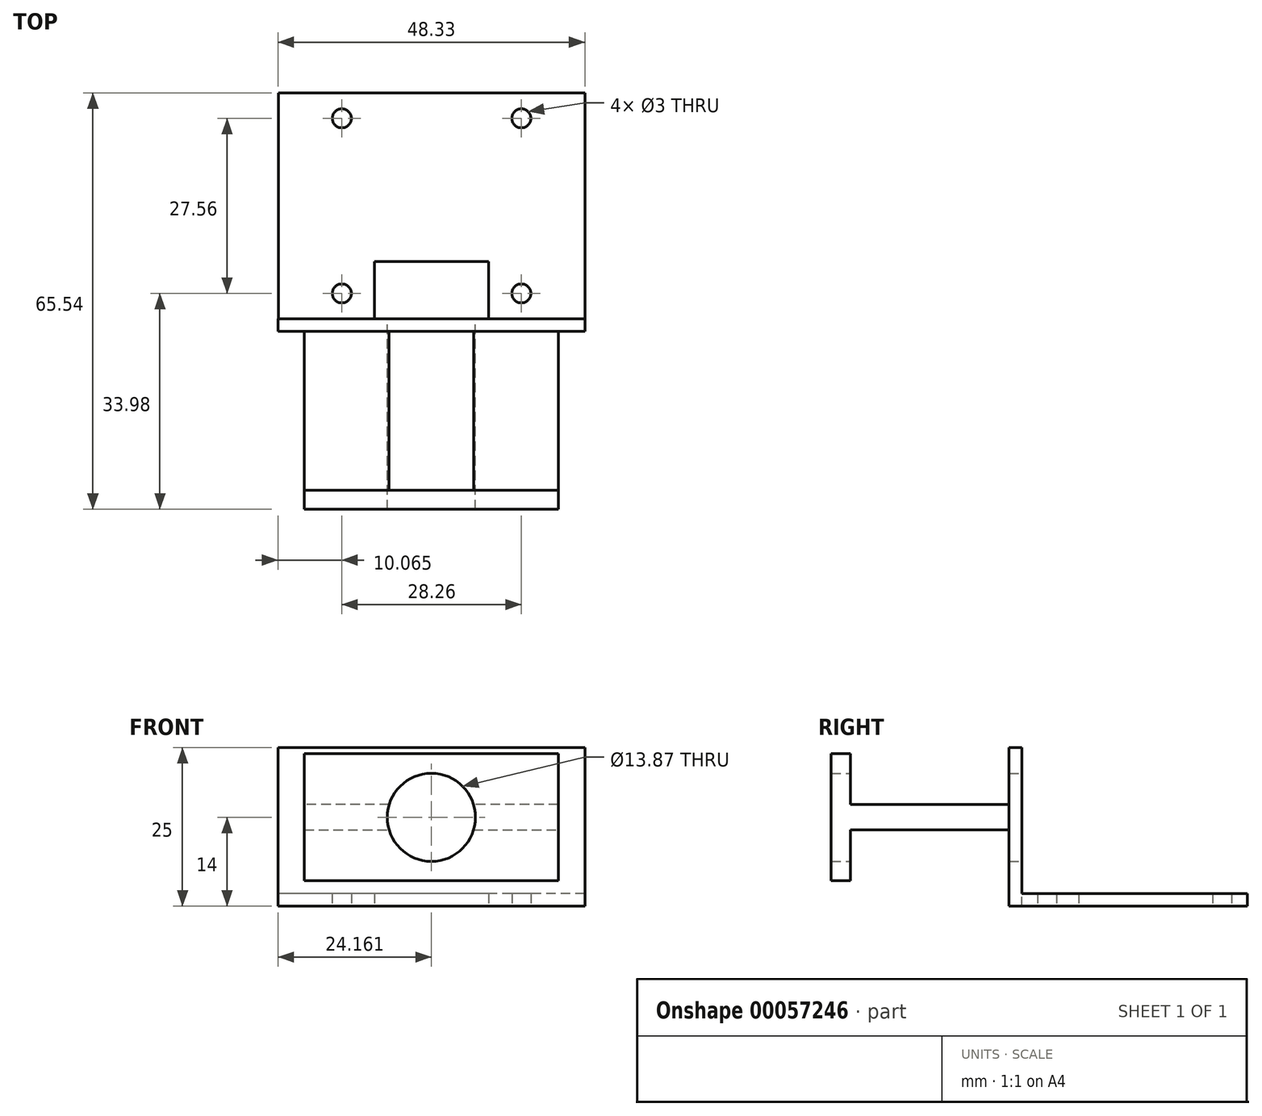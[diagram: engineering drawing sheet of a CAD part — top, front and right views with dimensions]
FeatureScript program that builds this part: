
annotation { "Feature Type Name" : "Feature", "Feature Type Description" : "" }
export const myFeature = defineFeature(function(context is Context, id is Id, definition is map)
    precondition{}
    {
        {
            var Q0;
            Q0=qCreatedBy(makeId("Top.planeOp"),FACE);
            var sketch = newSketch(context, id + "F0", { "sketchPlane" : qUnion([Q0])});
            skLineSegment(sketch, "E0.bottom", {"start": v(25, 16.6) * mm, "end": v(-23.25, 16.6) * mm});
            skLineSegment(sketch, "E0.top", {"start": v(25, -18.96) * mm, "end": v(-23.25, -18.96) * mm});
            skLineSegment(sketch, "E0.left", {"start": v(25, 16.6) * mm, "end": v(25, -18.96) * mm});
            skLineSegment(sketch, "E0.right", {"start": v(-23.25, 16.6) * mm, "end": v(-23.25, -18.96) * mm});
            skCircle(sketch, "E1", {"center": v(-13.25, 12.6) * mm, "radius": 1.5 * mm});
            skCircle(sketch, "E2", {"center": v(15, 12.6) * mm, "radius": 1.5 * mm});
            skLineSegment(sketch, "E3", {"start": v(-13.25, 16.6) * mm, "end": v(-13.25, 12.6) * mm, "construction": true});
            skLineSegment(sketch, "E4", {"start": v(-13.25, 12.6) * mm, "end": v(-23.25, 12.6) * mm, "construction": true});
            skLineSegment(sketch, "E5", {"start": v(15, 12.6) * mm, "end": v(15, 16.6) * mm, "construction": true});
            skLineSegment(sketch, "E6", {"start": v(15, 12.6) * mm, "end": v(25, 12.6) * mm, "construction": true});
            skCircle(sketch, "E7", {"center": v(-13.25, -14.96) * mm, "radius": 1.5 * mm});
            skCircle(sketch, "E8", {"center": v(15, -14.96) * mm, "radius": 1.5 * mm});
            skLineSegment(sketch, "E9", {"start": v(-13.25, -14.96) * mm, "end": v(-23.25, -14.96) * mm, "construction": true});
            skLineSegment(sketch, "E10", {"start": v(-13.25, -14.96) * mm, "end": v(-13.25, -18.96) * mm, "construction": true});
            skLineSegment(sketch, "E11", {"start": v(15, -14.96) * mm, "end": v(25, -14.96) * mm, "construction": true});
            skLineSegment(sketch, "E12", {"start": v(15, -14.96) * mm, "end": v(15, -18.96) * mm, "construction": true});
            skSolve(sketch);
        }
        {
            var Q0;
            Q0=makeQuery(id+"F0.imprint","IMPRINT",FACE,{"disambiguationData":[TD([[makeQuery(id+"F0.imprint","IMPRINT",EDGE,{"derivedFrom":sQuery(id+"F0.wireOp",EDGE,"E0.bottom")}),1.0]])]});
            extrude(context, id + "F1", {"entities" : qUnion([Q0]), "depth" : 2 * mm});
        }
        {
            var Q0;
            Q0=qCreatedBy(makeId("Top.planeOp"),FACE);
            var sketch = newSketch(context, id + "F2", { "sketchPlane" : qUnion([Q0])});
            skLineSegment(sketch, "E13.bottom", {"start": v(-23.32, -18.94) * mm, "end": v(25, -18.94) * mm});
            skLineSegment(sketch, "E13.top", {"start": v(-23.32, -20.94) * mm, "end": v(25, -20.94) * mm});
            skLineSegment(sketch, "E13.left", {"start": v(-23.32, -18.94) * mm, "end": v(-23.32, -20.94) * mm});
            skLineSegment(sketch, "E13.right", {"start": v(25, -18.94) * mm, "end": v(25, -20.94) * mm});
            skSolve(sketch);
        }
        {
            var Q0;
            Q0 = qSketchRegion(id + "F2", true);
            extrude(context, id + "F3", {"entities" : qUnion([Q0]), "operationType" : NewBodyOperationType.ADD, "depth" : 25 * mm});
        }
        {
            var Q0;
            Q0=qCreatedBy(makeId("Top.planeOp"),FACE);
            cPlane(context, id + "F4", {"entities" : qUnion([Q0]), "cplaneType" : CPlaneType.OFFSET, "offset" : 4 * mm, "oppositeDirection" : true, "width" : 150 * mm, "height" : 150 * mm});
        }
        {
            var Q0;
            Q0=makeQuery(id+"F7aZyVxxDA95Y1x_5.opBoolean","MERGE",FACE,{"derivedFrom":[makeQuery(id+"F1.opExtrude","CAP_FACE",FACE,{"disambiguationData":[OSD([sQuery(id+"F0.wireOp",EDGE,"E0.bottom"),sQuery(id+"F0.wireOp",EDGE,"E0.top"),sQuery(id+"F0.wireOp",EDGE,"E0.left"),sQuery(id+"F0.wireOp",EDGE,"E0.right"),sQuery(id+"F0.wireOp",EDGE,"E1"),sQuery(id+"F0.wireOp",EDGE,"E2"),sQuery(id+"F0.wireOp",EDGE,"E7"),sQuery(id+"F0.wireOp",EDGE,"E8")])],"isStart":true}),makeQuery(id+"F3.opExtrude","CAP_FACE",FACE,{"disambiguationData":[OSD([sQuery(id+"F2.wireOp",EDGE,"E13.bottom"),sQuery(id+"F2.wireOp",EDGE,"E13.top"),sQuery(id+"F2.wireOp",EDGE,"E13.left"),sQuery(id+"F2.wireOp",EDGE,"E13.right")])],"isStart":true})]});
            var sketch = newSketch(context, id + "F5", { "sketchPlane" : qUnion([Q0])});
            skLineSegment(sketch, "E14.bottom", {"start": v(-8.12, 9.94) * mm, "end": v(9.88, 9.94) * mm});
            skLineSegment(sketch, "E14.top", {"start": v(-8.12, 18.94) * mm, "end": v(9.88, 18.94) * mm});
            skLineSegment(sketch, "E14.left", {"start": v(-8.12, 9.94) * mm, "end": v(-8.12, 18.94) * mm});
            skLineSegment(sketch, "E14.right", {"start": v(9.88, 9.94) * mm, "end": v(9.88, 18.94) * mm});
            skLineSegment(sketch, "E15", {"start": v(-23.25, 18.94) * mm, "end": v(25, 18.94) * mm, "construction": true});
            skLineSegment(sketch, "E16", {"start": v(25, 18.94) * mm, "end": v(25.39, 18.73) * mm, "construction": true});
            skPoint(sketch, "E17", {"position": v(0.88, 18.94) * mm});
            skSolve(sketch);
        }
        {
            var Q0;
            Q0 = qSketchRegion(id + "F5", true);
            extrude(context, id + "F6", {"entities" : qUnion([Q0]), "operationType" : NewBodyOperationType.REMOVE, "oppositeDirection" : true, "depth" : 25 * mm});
        }
        {
            var Q0;
            Q0=makeQuery(id+"F3.opExtrude","SWEPT_FACE",FACE,{"disambiguationData":[OSD([sQuery(id+"F2.wireOp",EDGE,"E13.top")])]});
            var sketch = newSketch(context, id + "F7", { "sketchPlane" : qUnion([Q0])});
            skLineSegment(sketch, "E18.bottom", {"start": v(-19.16, 12) * mm, "end": v(20.84, 12) * mm});
            skLineSegment(sketch, "E18.top", {"start": v(-19.16, 2) * mm, "end": v(20.84, 2) * mm});
            skLineSegment(sketch, "E18.left", {"start": v(-19.16, 12) * mm, "end": v(-19.16, 16) * mm});
            skLineSegment(sketch, "E18.right", {"start": v(20.84, 12) * mm, "end": v(20.84, 16) * mm});
            skPoint(sketch, "E19", {"position": v(0.84, 2) * mm});
            skPoint(sketch, "E20.0", {"position": v(0.84, 1) * mm});
            skLineSegment(sketch, "E21", {"start": v(0.84, 2) * mm, "end": v(0.84, 1) * mm, "construction": true});
            skLineSegment(sketch, "E22", {"start": v(20.84, 16) * mm, "end": v(-19.16, 16) * mm});
            skLineSegment(sketch, "E23", {"start": v(20.84, 16) * mm, "end": v(20.84, 2) * mm, "construction": true});
            skLineSegment(sketch, "E24", {"start": v(-19.16, 16) * mm, "end": v(-19.16, 2) * mm, "construction": true});
            skPoint(sketch, "E25", {"position": v(20.84, 14) * mm});
            skPoint(sketch, "E26", {"position": v(0.84, 16) * mm});
            skPoint(sketch, "E27", {"position": v(0.84, 14) * mm});
            skLineSegment(sketch, "E28", {"start": v(0.84, 16) * mm, "end": v(0.84, 0) * mm, "construction": true});
            skSolve(sketch);
        }
        {
            var Q0;
            Q0 = qSketchRegion(id + "F7", true);
            extrude(context, id + "F8", {"entities" : qUnion([Q0]), "operationType" : NewBodyOperationType.ADD, "depth" : 25 * mm, "offsetDistance" : 25 * mm});
        }
        {
            var Q0;
            {var subQ0=sQuery(id+"F7.wireOp",EDGE,"E18.top");var subQ1=sQuery(id+"F7.wireOp",EDGE,"E18.bottom");var subQ10=sQuery(id+"F7.wireOp",EDGE,"E18.right");Q0=makeQuery(id+"F12.boolean.opBoolean","SPLIT",FACE,{"disambiguationData":[TD([makeQuery(id+"F8.opExtrude","SWEPT_FACE",FACE,{"disambiguationData":[OSD([subQ10])]})])],"derivedFrom":makeQuery(id+"F8.opExtrude","CAP_FACE",FACE,{"disambiguationData":[OSD([subQ1,subQ0,sQuery(id+"F7.wireOp",EDGE,"E18.left"),subQ10])],"isStart":false})});}
            var sketch = newSketch(context, id + "F9", { "sketchPlane" : qUnion([Q0])});
            skLineSegment(sketch, "E29.bottom", {"start": v(20.84, 24) * mm, "end": v(-19.16, 24) * mm});
            skLineSegment(sketch, "E29.top", {"start": v(20.84, 4) * mm, "end": v(-19.16, 4) * mm});
            skLineSegment(sketch, "E29.left", {"start": v(20.84, 24) * mm, "end": v(20.84, 4) * mm});
            skPoint(sketch, "E30", {"position": v(0.84, 4) * mm});
            skPoint(sketch, "E31", {"position": v(0.84, 24) * mm});
            skPoint(sketch, "E32", {"position": v(0.84, 14) * mm});
            skLineSegment(sketch, "E33", {"start": v(-19.16, 4) * mm, "end": v(-19.16, 24) * mm});
            skLineSegment(sketch, "E34", {"start": v(0.84, 4) * mm, "end": v(0.84, 24) * mm, "construction": true});
            skSolve(sketch);
        }
        {
            var Q0;
            Q0 = qSketchRegion(id + "F9", true);
            extrude(context, id + "F10", {"entities" : qUnion([Q0]), "operationType" : NewBodyOperationType.ADD, "depth" : 3 * mm});
        }
        {
            var Q0;
            Q0=makeQuery(id+"F7.imprint","IMPRINT",FACE,{"disambiguationData":[TD([[makeQuery(id+"F7.imprint","IMPRINT",EDGE,{"derivedFrom":sQuery(id+"F7.wireOp",EDGE,"E18.bottom")}),1.0]])]});
            var sketch = newSketch(context, id + "F11", { "sketchPlane" : qUnion([Q0])});
            skPoint(sketch, "E35.0", {"position": v(0.84, 14) * mm});
            skCircle(sketch, "E36", {"center": v(0.84, 14) * mm, "radius": 6.94 * mm});
            skSolve(sketch);
        }
        {
            var Q0;
            Q0 = qSketchRegion(id + "F11", true);
            extrude(context, id + "F12", {"entities" : qUnion([Q0]), "operationType" : NewBodyOperationType.REMOVE, "depth" : 30 * mm, "offsetDistance" : 25 * mm});
        }
        {
            var Q0;
            Q0 = qSketchRegion(id + "F11", true);
            extrude(context, id + "F13", {"entities" : qUnion([Q0]), "operationType" : NewBodyOperationType.REMOVE, "oppositeDirection" : true, "depth" : 25 * mm});
        }
    });
